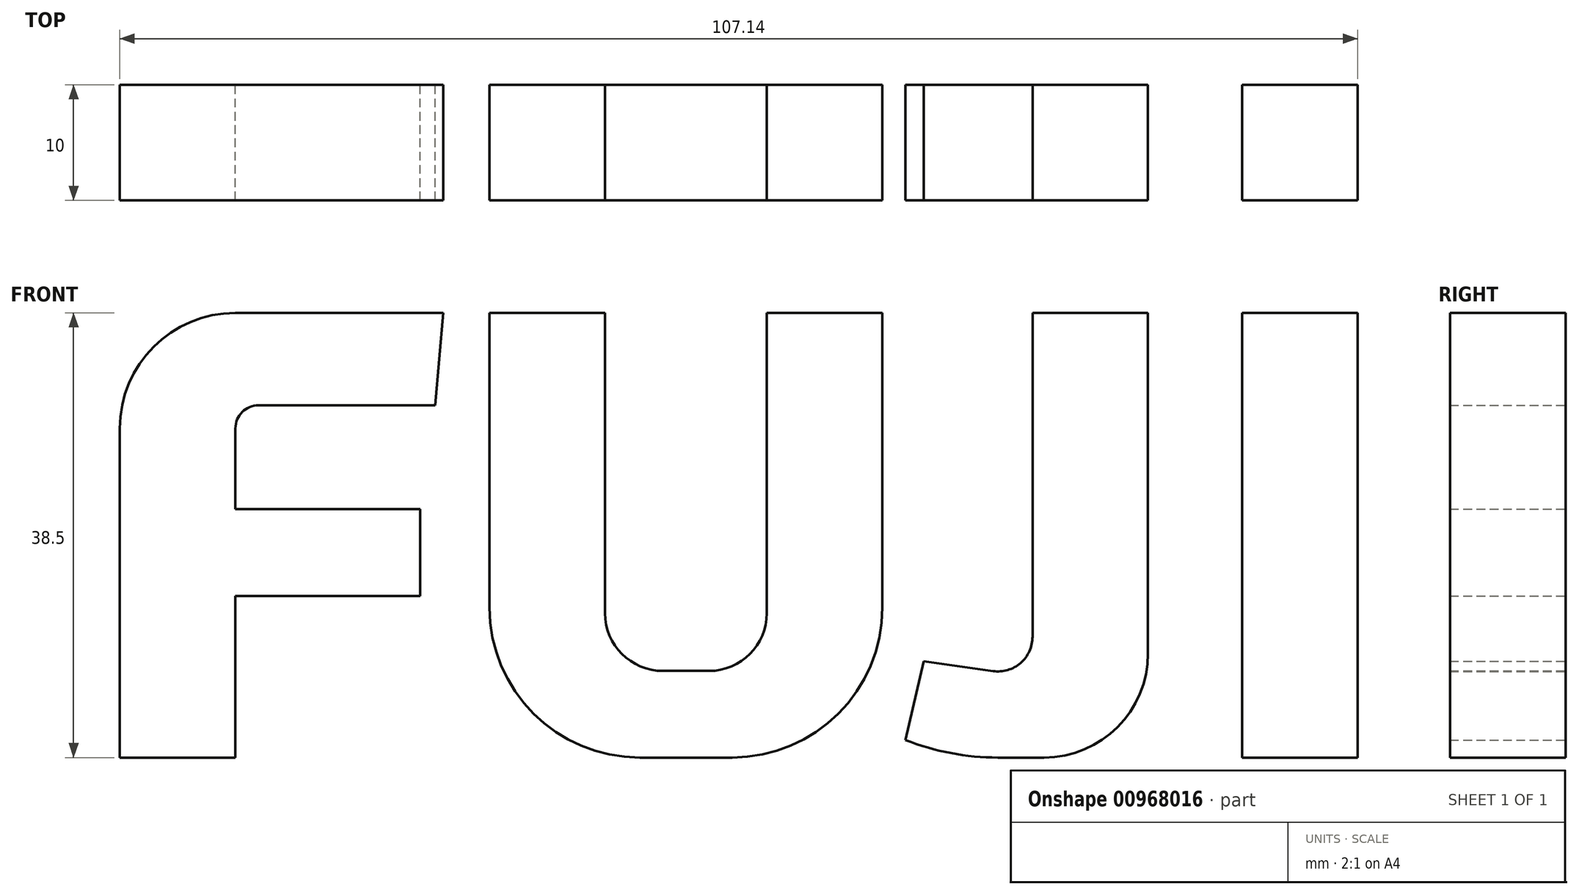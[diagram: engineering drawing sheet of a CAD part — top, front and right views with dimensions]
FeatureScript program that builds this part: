
annotation { "Feature Type Name" : "Feature", "Feature Type Description" : "" }
export const myFeature = defineFeature(function(context is Context, id is Id, definition is map)
    precondition{}
    {
        {
            var Q0;
            Q0=qCreatedBy(makeId("Front.planeOp"),FACE);
            var sketch = newSketch(context, id + "F0", { "sketchPlane" : qUnion([Q0])});
            skLineSegment(sketch, "E0.bottom", {"start": v(28.5, 39) * mm, "end": v(10.5, 39) * mm});
            skLineSegment(sketch, "E0.top", {"start": v(10.5, 0.5) * mm, "end": v(0.5, 0.5) * mm});
            skLineSegment(sketch, "E0.right", {"start": v(0.5, 29) * mm, "end": v(0.5, 0.5) * mm});
            skPoint(sketch, "E1.visualSharp", {"position": v(0.5, 39) * mm});
            skArc(sketch, "E1.filletArc", {"start": v(10.5, 39) * mm, "mid": v(3.43, 36.07) * mm, "end": v(0.5, 29) * mm});
            skLineSegment(sketch, "E2.bottom", {"start": v(27.8, 31) * mm, "end": v(12.5, 31) * mm});
            skLineSegment(sketch, "E2.right", {"start": v(10.5, 29) * mm, "end": v(10.5, 22) * mm});
            skPoint(sketch, "E3.visualSharp", {"position": v(10.5, 31) * mm});
            skArc(sketch, "E3.filletArc", {"start": v(12.5, 31) * mm, "mid": v(11.09, 30.41) * mm, "end": v(10.5, 29) * mm});
            skLineSegment(sketch, "E4", {"start": v(28.5, 39) * mm, "end": v(27.8, 31) * mm});
            skLineSegment(sketch, "E5.bottom", {"start": v(10.5, 22) * mm, "end": v(26.5, 22) * mm});
            skLineSegment(sketch, "E5.top", {"start": v(10.5, 14.5) * mm, "end": v(26.5, 14.5) * mm});
            skLineSegment(sketch, "E5.right", {"start": v(26.5, 22) * mm, "end": v(26.5, 14.5) * mm});
            skLineSegment(sketch, "E6.trimOffspring", {"start": v(10.5, 14.5) * mm, "end": v(10.5, 0.5) * mm});
            skLineSegment(sketch, "E7.top", {"start": v(47.5, 8) * mm, "end": v(51.5, 8) * mm});
            skLineSegment(sketch, "E7.left", {"start": v(42.5, 39) * mm, "end": v(42.5, 13) * mm});
            skLineSegment(sketch, "E7.right", {"start": v(56.5, 39) * mm, "end": v(56.5, 13) * mm});
            skPoint(sketch, "E8.visualSharp", {"position": v(42.5, 8) * mm});
            skArc(sketch, "E8.filletArc", {"start": v(42.5, 13) * mm, "mid": v(43.96, 9.46) * mm, "end": v(47.5, 8) * mm});
            skPoint(sketch, "E9.visualSharp", {"position": v(56.5, 8) * mm});
            skArc(sketch, "E9.filletArc", {"start": v(51.5, 8) * mm, "mid": v(55.04, 9.46) * mm, "end": v(56.5, 13) * mm});
            skLineSegment(sketch, "E10", {"start": v(32.5, 39) * mm, "end": v(32.5, 13.5) * mm});
            skLineSegment(sketch, "E11", {"start": v(45.5, 0.5) * mm, "end": v(53.5, 0.5) * mm});
            skLineSegment(sketch, "E12", {"start": v(66.5, 13.5) * mm, "end": v(66.5, 39) * mm});
            skLineSegment(sketch, "E13", {"start": v(32.5, 39) * mm, "end": v(42.5, 39) * mm});
            skLineSegment(sketch, "E14", {"start": v(56.5, 39) * mm, "end": v(66.5, 39) * mm});
            skPoint(sketch, "E15.visualSharp", {"position": v(32.5, 0.5) * mm});
            skArc(sketch, "E15.filletArc", {"start": v(32.5, 13.5) * mm, "mid": v(36.3, 4.3) * mm, "end": v(45.5, 0.5) * mm});
            skPoint(sketch, "E16.visualSharp", {"position": v(66.5, 0.5) * mm});
            skArc(sketch, "E16.filletArc", {"start": v(53.5, 0.5) * mm, "mid": v(62.7, 4.3) * mm, "end": v(66.5, 13.5) * mm});
            skLineSegment(sketch, "E17.bottom", {"start": v(79.5, 39) * mm, "end": v(89.5, 39) * mm});
            skLineSegment(sketch, "E17.top", {"start": v(76.5, 0.5) * mm, "end": v(80.5, 0.5) * mm});
            skLineSegment(sketch, "E17.right", {"start": v(89.5, 39) * mm, "end": v(89.5, 9.5) * mm});
            skPoint(sketch, "E18.visualSharp", {"position": v(89.5, 0.5) * mm});
            skArc(sketch, "E18.filletArc", {"start": v(80.5, 0.5) * mm, "mid": v(86.86, 3.14) * mm, "end": v(89.5, 9.5) * mm});
            skArc(sketch, "E19", {"start": v(76.5, 0.5) * mm, "mid": v(72.43, 0.88) * mm, "end": v(68.5, 2.03) * mm});
            skLineSegment(sketch, "E20", {"start": v(68.5, 2.03) * mm, "end": v(70.1, 8.84) * mm});
            skLineSegment(sketch, "E21", {"start": v(79.5, 39) * mm, "end": v(79.5, 10.96) * mm});
            skArc(sketch, "E22", {"start": v(79.5, 10.96) * mm, "mid": v(78.47, 8.69) * mm, "end": v(76.08, 7.99) * mm});
            skLineSegment(sketch, "E23", {"start": v(76.08, 7.99) * mm, "end": v(70.1, 8.84) * mm});
            skLineSegment(sketch, "E24.bottom", {"start": v(97.64, 39) * mm, "end": v(107.64, 39) * mm});
            skLineSegment(sketch, "E24.top", {"start": v(97.64, 0.5) * mm, "end": v(107.64, 0.5) * mm});
            skLineSegment(sketch, "E24.left", {"start": v(97.64, 39) * mm, "end": v(97.64, 0.5) * mm});
            skLineSegment(sketch, "E24.right", {"start": v(107.64, 39) * mm, "end": v(107.64, 0.5) * mm});
            skSolve(sketch);
        }
        {
            var Q0;
            Q0 = qSketchRegion(id + "F0", true);
            extrude(context, id + "F1", {"entities" : qUnion([Q0]), "depth" : 10 * mm, "offsetDistance" : 25 * mm});
        }
    });
